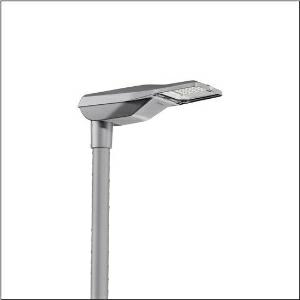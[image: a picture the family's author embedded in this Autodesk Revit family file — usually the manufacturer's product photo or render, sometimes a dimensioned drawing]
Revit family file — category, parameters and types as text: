
# Revit family: streetlight_sl_21_iq_micro___st1_0a_5xe1d21d08cb_1078
name_source: partatom
category: Lighting Fixtures
units: mm (PartAtom-declared; Revit-internal decimal feet)

## family parameters
Cut with Voids When Loaded = No
Host = Face
Light Source = No
Part Type = Normal
Room Calculation Point = No
Round Connector Dimension = Use Diameter
Shared = No

## types (1)
- --- (1 x LED, 2380 lm, 19.4 W, 2200K)
    Apparent Load = 19 VA
    CIE Flux Codes = 37 72 97 100 100
    Color Rendering = 70
    Color Temperature = 2200K
    Default Elevation = 1800 mm
    Description = Streetlight SL 21 iQ micro, mast luminaire, primary light control with lens, of PMMA, primary optical cover: cover, of toughened safety glass, transparent, light distribution: ST1.0a, light emission: direct distribution, primary light characteristic: asymmetric, installation type: post-top, side-entry, LED, High Power LED, rated luminous flux: 2.380lm, luminous efficacy: 123lm/W, light colour: 722, colour temperature: 2200K, control gear: iQ-Comfort, control: Auto-Match, Temp-Guard, Lumen-Switch, Night-Set, Smart-Wire, Light-Fading, Desk-Remote (wireless, voltage-free reading and setting of iQ features in the workshop via application-optimized NFC function/RFID function), optimised constant luminous flux control (CLO 2.0), pre-setting: linear dimming characteristic, mains connection: 220..240V, AC, 50/60Hz, start of lifetime: 19W, end of service life: 20W, reduction: 10W, luminaire housing, of diecast aluminium, powder-coated, SITECO metallic grey (DB 702S), corrosivity category C5 high according to DIN EN ISO 12944, please order mast flange separately, inclination adjustable: 0°, 5°, 10°, 15°, sealing non-destructively replaceable, multi-level sealing system, length: 528mm, width: 235mm, height: 110mm, mast flange for spigot size: 42mm (side-entry): 5XC10008XM4, 60/48mm (side-entry/post-top): 5XC10108XM2, 76/60mm (side-entry/post-top): 5XC10108XM1, protection rating (complete): IP66, insulation class (complete): insulation class II (safety insulation), certification: CE, ENEC, ENEC+, VDE, impact resistance: IK10, permissible operating ambient temperature for outdoor applications: -40..+50°C, standard-compliant lighting for roads and squares, packaging unit: 1 piece

Light Distribution: ST1.0a
    Height = 110 mm
    Lamp = 1 x LED
    Lamp Light Flux = 2380 lm
    Lamp Power = 19.4 W
    Lamp count = 1
    Length = 528 mm
    Luminous efficacy = 123 lm/W
    Manufacturer = Siteco
    ModVariant = No
    Model = 5XE1D21D08CB
    Number of Poles = 1
    OnlyDefault = Yes
    Power Factor = 1
    Product Name = Streetlight SL 21 iQ micro | ST1.0a
    Product group = mast luminaire | pylon top
    ProductGroupID = 6100
    Protection Class = Protection class II
    Protection Degree = IP 66
    RLX_Detail_Level = 1
    RLX_Emergency_Light_Flux = 0 lm
    RLX_Emergency_Type = 0
    RLX_Emergency_Type_DB = No
    RlxData = <blob elided: 98649 chars, md5=f852ec0e>
    Socket = socket
    Standby Power = 0 W
    System Light Flux = 2380 lm
    System Power = 19 W
    Type Comments = factory setting: luminous flux: 100 % | dim-lin: 254 | 387 mA
    Type Image = l_1006881.jpg
    URL = http://relux.com
    VarID = @adj_138855
    Voltage = 0 V
    Weight = 0.00 kg
    Width = 235 mm

## geometry (parser evidence)
native form markers: Blend x4, Sweep x12
no freeform markers — native parametric forms only
